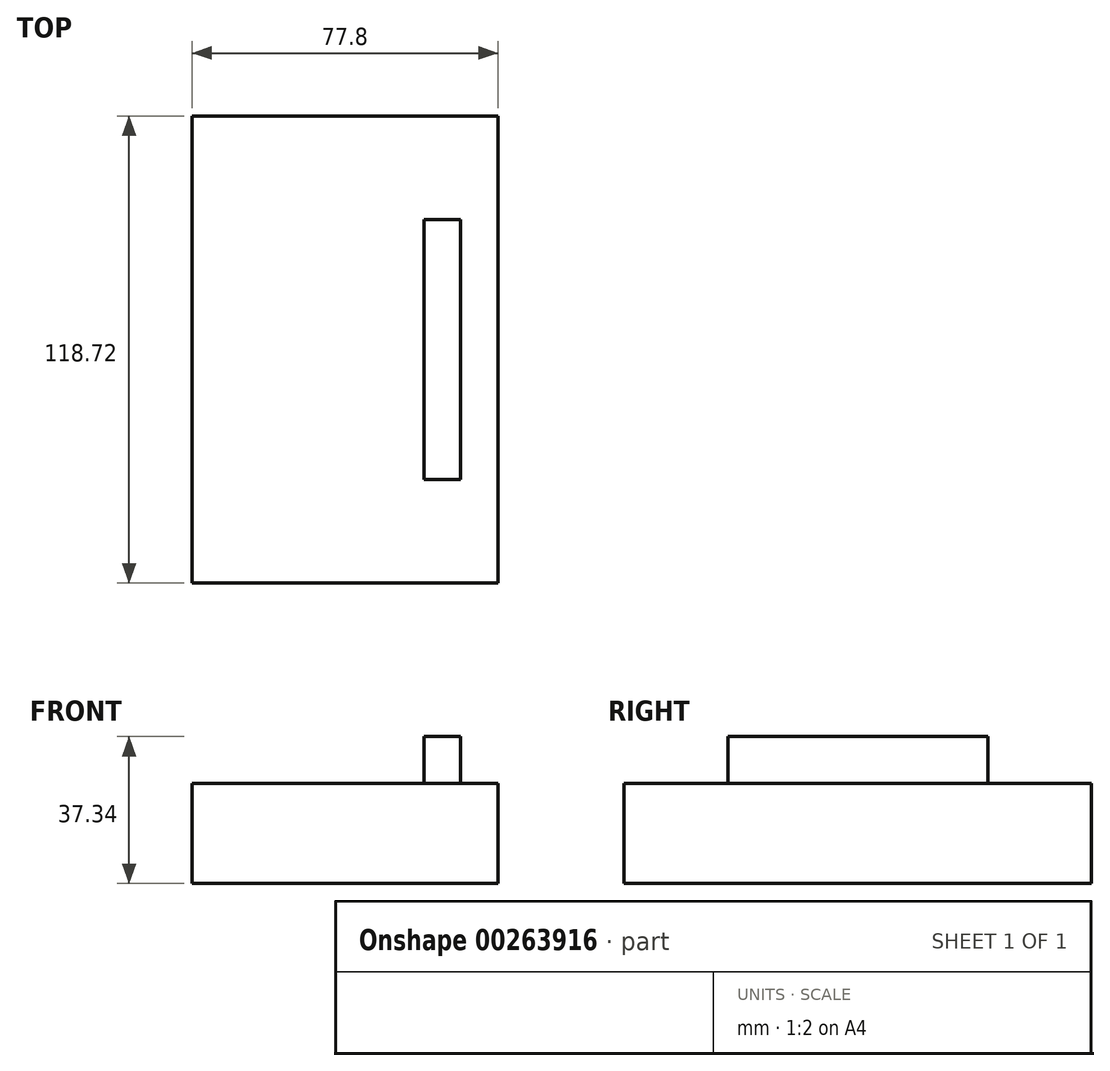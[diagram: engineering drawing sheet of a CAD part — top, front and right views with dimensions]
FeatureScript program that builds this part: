
annotation { "Feature Type Name" : "Feature", "Feature Type Description" : "" }
export const myFeature = defineFeature(function(context is Context, id is Id, definition is map)
    precondition{}
    {
        {
            var Q0;
            Q0=qCreatedBy(makeId("Top.planeOp"),FACE);
            var sketch = newSketch(context, id + "F0", { "sketchPlane" : qUnion([Q0])});
            skLineSegment(sketch, "E0.bottom", {"start": v(-38.9, 59.36) * mm, "end": v(38.9, 59.36) * mm});
            skLineSegment(sketch, "E0.top", {"start": v(-38.9, -59.36) * mm, "end": v(38.9, -59.36) * mm});
            skLineSegment(sketch, "E0.left", {"start": v(-38.9, 59.36) * mm, "end": v(-38.9, -59.36) * mm});
            skLineSegment(sketch, "E0.right", {"start": v(38.9, 59.36) * mm, "end": v(38.9, -59.36) * mm});
            skPoint(sketch, "E0.middle", {"position": v(0, 0) * mm});
            skPoint(sketch, "E1.middle", {"position": v(24.7, 0) * mm});
            skPoint(sketch, "E1.bottom.end.orphan", {"position": v(29.5, 33) * mm});
            skPoint(sketch, "E1.bottom.start.orphan", {"position": v(19.91, 33) * mm});
            skPoint(sketch, "E1.top.end.orphan", {"position": v(29.5, -33) * mm});
            skPoint(sketch, "E1.top.start.orphan", {"position": v(19.91, -33) * mm});
            skSolve(sketch);
        }
        {
            var Q0;
            Q0=makeQuery(id+"F0.imprint","IMPRINT",FACE,{"disambiguationData":[TD([[makeQuery(id+"F0.imprint","IMPRINT",EDGE,{"derivedFrom":sQuery(id+"F0.wireOp",EDGE,"E0.bottom")}),-1.0]])]});
            var sketch = newSketch(context, id + "F1", { "sketchPlane" : qUnion([Q0])});
            skLineSegment(sketch, "E2.bottom", {"start": v(20.1, 33) * mm, "end": v(29.31, 33) * mm});
            skLineSegment(sketch, "E2.top", {"start": v(20.1, -33) * mm, "end": v(29.31, -33) * mm});
            skLineSegment(sketch, "E2.left", {"start": v(20.1, 33) * mm, "end": v(20.1, -33) * mm});
            skLineSegment(sketch, "E2.right", {"start": v(29.31, 33) * mm, "end": v(29.31, -33) * mm});
            skPoint(sketch, "E2.middle", {"position": v(24.7, 0) * mm});
            skSolve(sketch);
        }
        {
            var Q0;
            Q0 = qSketchRegion(id + "F0", true);
            extrude(context, id + "F2", {"entities" : qUnion([Q0]), "depth" : 25.4 * mm});
        }
        {
            var Q0;
            Q0 = qSketchRegion(id + "F1", true);
            extrude(context, id + "F3", {"entities" : qUnion([Q0]), "operationType" : NewBodyOperationType.ADD, "depth" : 37.34 * mm});
        }
    });
